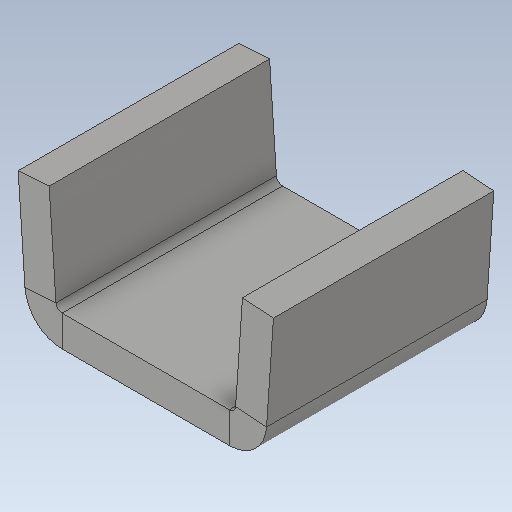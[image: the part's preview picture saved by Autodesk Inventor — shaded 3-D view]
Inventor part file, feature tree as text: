
AUTODESK INVENTOR PART (.ipt)
format: ipt  version: 2020.1 (Build 241239000, 239)  size: 126,464 bytes
history: native  units: mm
features: sheet_metal_op x4, sketch x2, other x2
ambient origin geometry x8: Origin, YZ Plane, XZ Plane, XY Plane, X Axis, Y Axis, Z Axis, Center Point
bodies: Solid1 (feature_tree)
feature tree (8):
  sheet_metal_op  "Face1"
  sheet_metal_op  "Flange1"
  sketch  "Sketch1"  dims[d0=35.5mm]
  other  "Plate1"
  sketch  "Sketch2"  dims[d1=5.0mm d2=5.0mm d3=2.5mm d4=10.0mm d5=1.0mm d6=21.37mm d7=15.009832mm d8=1.0mm d9=20.0mm d10=5.0mm d11=1.0mm d12=38.128mm]
  other  "Plate2"
  sheet_metal_op  "Bend1"
  sheet_metal_op  "Corner1"
